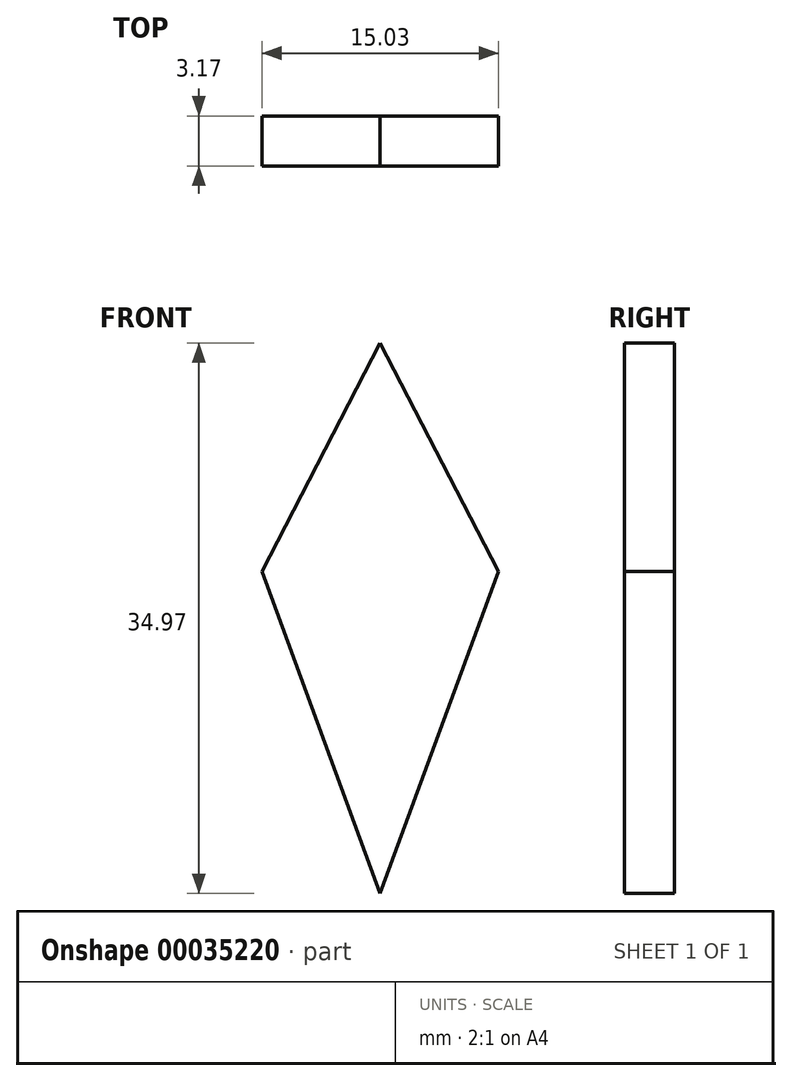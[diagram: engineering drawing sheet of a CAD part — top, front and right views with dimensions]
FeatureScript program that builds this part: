
annotation { "Feature Type Name" : "Feature", "Feature Type Description" : "" }
export const myFeature = defineFeature(function(context is Context, id is Id, definition is map)
    precondition{}
    {
        {
            var Q0;
            Q0=qCreatedBy(makeId("Front.planeOp"),FACE);
            var sketch = newSketch(context, id + "F0", { "sketchPlane" : qUnion([Q0])});
            skLineSegment(sketch, "E0", {"start": v(-17.67, 40.53) * mm, "end": v(-25.18, 26.02) * mm});
            skLineSegment(sketch, "E1", {"start": v(-25.18, 26.02) * mm, "end": v(-17.67, 5.56) * mm});
            skLineSegment(sketch, "E2", {"start": v(-17.67, 5.56) * mm, "end": v(-17.67, 40.53) * mm});
            skLineSegment(sketch, "E3.MirrorCS", {"start": v(-17.67, 40.53) * mm, "end": v(-10.15, 26.02) * mm});
            skLineSegment(sketch, "E4.MirrorCS", {"start": v(-10.15, 26.02) * mm, "end": v(-17.67, 5.56) * mm});
            skSolve(sketch);
        }
        {
            var Q0;
            Q0=makeQuery(id+"F0.imprint","IMPRINT",FACE,{"disambiguationData":[TD([[makeQuery(id+"F0.imprint","IMPRINT",EDGE,{"derivedFrom":sQuery(id+"F0.wireOp",EDGE,"E0")}),1.0]])]});
            var Q1;
            Q1=makeQuery(id+"F0.imprint","IMPRINT",FACE,{"disambiguationData":[TD([[makeQuery(id+"F0.imprint","IMPRINT",EDGE,{"derivedFrom":sQuery(id+"F0.wireOp",EDGE,"E2")}),-1.0]])]});
            extrude(context, id + "F1", {"entities" : qUnion([Q0, Q1]), "depth" : 3.17 * mm});
        }
    });
